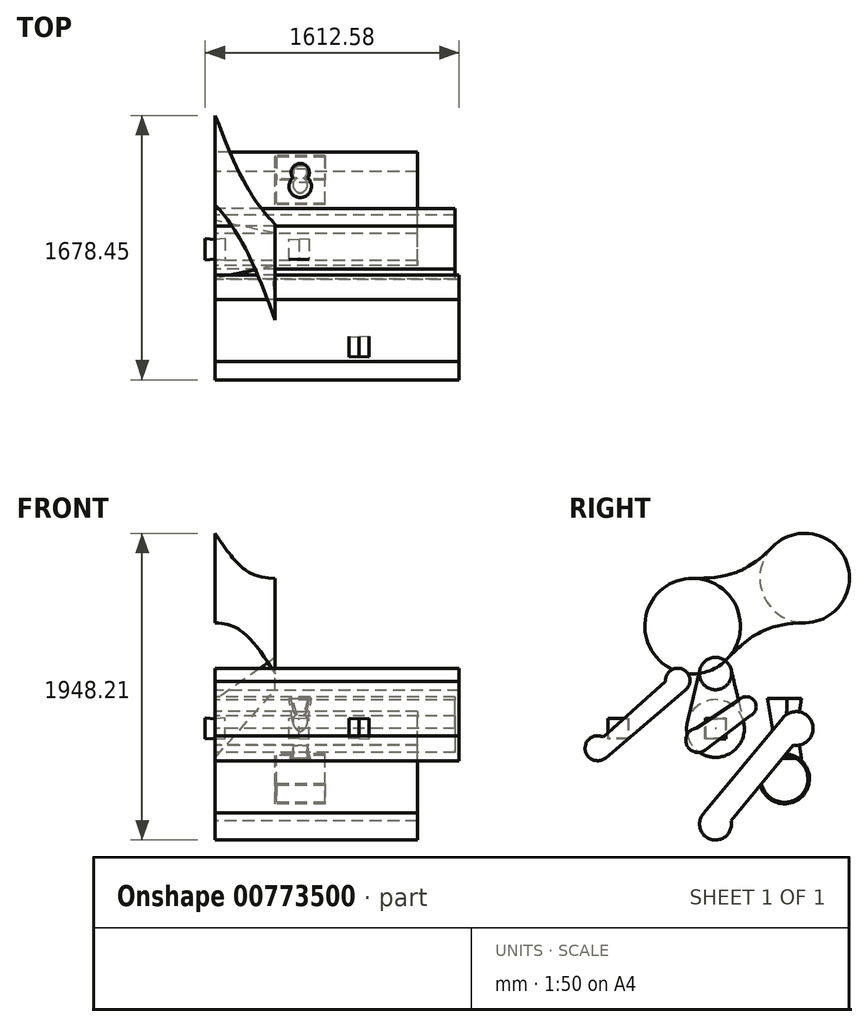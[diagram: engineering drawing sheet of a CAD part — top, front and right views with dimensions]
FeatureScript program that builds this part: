
annotation { "Feature Type Name" : "Feature", "Feature Type Description" : "" }
export const myFeature = defineFeature(function(context is Context, id is Id, definition is map)
    precondition{}
    {
        {
            var Q0;
            Q0=qCreatedBy(makeId("Right.planeOp"),FACE);
            var sketch = newSketch(context, id + "F0", { "sketchPlane" : qUnion([Q0])});
            skArc(sketch, "E0", {"start": v(218.18, 79.74) * mm, "mid": v(247.67, 174.38) * mm, "end": v(148.83, 181.9) * mm});
            skCircle(sketch, "E1", {"center": v(-111.14, -74.72) * mm, "radius": 77.61 * mm});
            skLineSegment(sketch, "E2", {"start": v(218.18, 79.74) * mm, "end": v(-63.95, -136.34) * mm});
            skPoint(sketch, "E3.end.orphan", {"position": v(-138.22, 0) * mm});
            skLineSegment(sketch, "E4", {"start": v(-125.4, 1.57) * mm, "end": v(148.83, 181.9) * mm});
            skSolve(sketch);
        }
        {
            var Q0;
            Q0 = qSketchRegion(id + "F0", true);
            extrude(context, id + "F1", {"entities" : qUnion([Q0]), "depth" : 1524 * mm, "offsetDistance" : 25.4 * mm});
        }
        {
            var Q0;
            Q0=qCreatedBy(makeId("Right.planeOp"),FACE);
            var sketch = newSketch(context, id + "F2", { "sketchPlane" : qUnion([Q0])});
            skCircle(sketch, "E5", {"center": v(-748.62, -125.15) * mm, "radius": 79.46 * mm});
            skCircle(sketch, "E6", {"center": v(-240.04, 305.06) * mm, "radius": 77.83 * mm});
            skLineSegment(sketch, "E7", {"start": v(-192.7, 243.28) * mm, "end": v(-697.14, -185.68) * mm});
            skLineSegment(sketch, "E8", {"start": v(-317.74, 300.55) * mm, "end": v(-712.8, -54.22) * mm});
            skSolve(sketch);
        }
        {
            var Q0;
            Q0 = qSketchRegion(id + "F2", true);
            extrude(context, id + "F3", {"entities" : qUnion([Q0]), "depth" : 1549.08 * mm, "offsetDistance" : 25.4 * mm});
        }
        {
            var Q0;
            Q0=qCreatedBy(makeId("Right.planeOp"),FACE);
            var sketch = newSketch(context, id + "F4", { "sketchPlane" : qUnion([Q0])});
            skCircle(sketch, "E9", {"center": v(511.78, 0) * mm, "radius": 107.3 * mm});
            skCircle(sketch, "E10", {"center": v(0, -606.9) * mm, "radius": 101.16 * mm});
            skLineSegment(sketch, "E11", {"start": v(-72.14, -535.98) * mm, "end": v(429.2, 68.5) * mm});
            skLineSegment(sketch, "E12", {"start": v(99.25, -587.3) * mm, "end": v(493.66, -105.75) * mm});
            skSolve(sketch);
        }
        {
            var Q0;
            Q0 = qSketchRegion(id + "F4", true);
            extrude(context, id + "F5", {"entities" : qUnion([Q0]), "depth" : 1284.3 * mm, "offsetDistance" : 25.4 * mm});
        }
        {
            var Q0;
            Q0=qCreatedBy(makeId("Right.planeOp"),FACE);
            cPlane(context, id + "F6", {"entities" : qUnion([Q0]), "cplaneType" : CPlaneType.OFFSET, "offset" : 381 * mm, "width" : 152.4 * mm, "height" : 152.4 * mm});
        }
        {
            var Q0;
            Q0=qCreatedBy(makeId("Right.planeOp"),FACE);
            var sketch = newSketch(context, id + "F7", { "sketchPlane" : qUnion([Q0])});
            skCircle(sketch, "E13", {"center": v(566.14, 955.92) * mm, "radius": 284.23 * mm});
            skSolve(sketch);
        }
        {
            var Q0;
            Q0=qCreatedBy(id+"F6.planeOp",FACE);
            var sketch = newSketch(context, id + "F8", { "sketchPlane" : qUnion([Q0])});
            skCircle(sketch, "E14", {"center": v(-145.34, 650.7) * mm, "radius": 303.5 * mm});
            skSolve(sketch);
        }
        {
            var Q1;
            Q1=makeQuery(id+"F7.imprint","IMPRINT",FACE,{"disambiguationData":[TD([[makeQuery(id+"F7.imprint","IMPRINT",EDGE,{"derivedFrom":sQuery(id+"F7.wireOp",EDGE,"E13")}),1.0]])]});
            var Q2;
            Q2=makeQuery(id+"F8.imprint","IMPRINT",FACE,{"disambiguationData":[TD([[makeQuery(id+"F8.imprint","IMPRINT",EDGE,{"derivedFrom":sQuery(id+"F8.wireOp",EDGE,"E14")}),1.0]])]});
            loft(context, id + "F9", {"operationType" : NewBodyOperationType.ADD, "sheetProfilesArray" : [{ "sheetProfileEntities" : qUnion([Q1]) }, { "sheetProfileEntities" : qUnion([Q2]) }]});
        }
        {
            var Q0;
            Q0=qCreatedBy(id+"F6.planeOp",FACE);
            var sketch = newSketch(context, id + "F10", { "sketchPlane" : qUnion([Q0])});
            skCircle(sketch, "E15", {"center": v(0, 348.94) * mm, "radius": 102.64 * mm});
            skLineSegment(sketch, "E16", {"start": v(0, 348.94) * mm, "end": v(0, 0) * mm, "construction": true});
            skCircle(sketch, "E17", {"center": v(0, 0) * mm, "radius": 183.3 * mm});
            skSolve(sketch);
        }
        {
            var Q0;
            Q0=qCreatedBy(makeId("Right.planeOp"),FACE);
            var sketch = newSketch(context, id + "F11", { "sketchPlane" : qUnion([Q0])});
            skCircle(sketch, "E18.0", {"center": v(0, 0) * mm, "radius": 183.3 * mm});
            skSolve(sketch);
        }
        {
            var Q0;
            Q0=makeQuery(id+"F11.imprint","IMPRINT",FACE,{"disambiguationData":[TD([[makeQuery(id+"F11.imprint","IMPRINT",EDGE,{"derivedFrom":sQuery(id+"F11.wireOp",EDGE,"E18.0")}),1.0]])]});
            var Q1;
            Q1=makeQuery(id+"F10.imprint","IMPRINT",FACE,{"disambiguationData":[TD([[makeQuery(id+"F10.imprint","IMPRINT",EDGE,{"derivedFrom":sQuery(id+"F10.wireOp",EDGE,"E15")}),1.0]])]});
            loft(context, id + "F12", {"sheetProfilesArray" : [{ "sheetProfileEntities" : qUnion([Q0]) }, { "sheetProfileEntities" : qUnion([Q1]) }]});
        }
        {
            var Q0;
            Q0=qCreatedBy(id+"F6.planeOp",FACE);
            var sketch = newSketch(context, id + "F13", { "sketchPlane" : qUnion([Q0])});
            skLineSegment(sketch, "E19", {"start": v(0, 0) * mm, "end": v(438.16, -319.98) * mm, "construction": true});
            skCircle(sketch, "E20", {"center": v(438.16, -319.98) * mm, "radius": 158.42 * mm});
            skSolve(sketch);
        }
        {
            var Q0;
            Q0 = qSketchRegion(id + "F13", true);
            extrude(context, id + "F14", {"entities" : qUnion([Q0]), "depth" : 316.85 * mm, "offsetDistance" : 25.4 * mm});
        }
        {
            var Q0;
            Q0=makeQuery(id+"F14.opExtrude","CAP_FACE",FACE,{"disambiguationData":[OSD([sQuery(id+"F13.wireOp",EDGE,"E20")])],"isStart":false});
            shell(context, id + "F15", {"entities" : qUnion([Q0]), "thickness" : 9.52 * mm});
        }
        {
            var Q0;
            Q0=qCreatedBy(makeId("Top.planeOp"),FACE);
            var sketch = newSketch(context, id + "F16", { "sketchPlane" : qUnion([Q0])});
            skLineSegment(sketch, "E21", {"start": v(381, 596.58) * mm, "end": v(697.85, 596.58) * mm});
            skLineSegment(sketch, "E22", {"start": v(697.85, 279.74) * mm, "end": v(381, 279.74) * mm});
            skCircle(sketch, "E23", {"center": v(539.42, 400.75) * mm, "radius": 39.96 * mm});
            skPoint(sketch, "E23.centerSnap0", {"position": v(539.42, 596.58) * mm});
            skCircle(sketch, "E24", {"center": v(539.42, 487.87) * mm, "radius": 26.5 * mm});
            skSolve(sketch);
        }
        {
            var Q0;
            Q0 = qSketchRegion(id + "F16", true);
            extrude(context, id + "F17", {"entities" : qUnion([Q0]), "operationType" : NewBodyOperationType.ADD, "endBound" : BoundingType.SYMMETRIC, "depth" : 381 * mm, "offsetDistance" : 25.4 * mm, "hasDraft" : true, "draftAngle" : 9.38 * degree});
        }
        {
            var Q0;
            Q0=qCreatedBy(makeId("Top.planeOp"),FACE);
            var sketch = newSketch(context, id + "F18", { "sketchPlane" : qUnion([Q0])});
            skLineSegment(sketch, "E25", {"start": v(0, 0) * mm, "end": v(0, -609.6) * mm, "construction": true});
            skLineSegment(sketch, "E26", {"start": v(0, -609.6) * mm, "end": v(914.4, -609.6) * mm, "construction": true});
            skSolve(sketch);
        }
        {
            var Q0;
            Q0=qCreatedBy(makeId("Right.planeOp"),FACE);
            var Q1;
            Q1=sQuery(id+"F18.wireOp",VERTEX,"E26.end");
            cPlane(context, id + "F19", {"entities" : qUnion([Q0, Q1]), "cplaneType" : CPlaneType.PLANE_POINT, "offset" : 25.4 * mm, "width" : 152.4 * mm, "height" : 152.4 * mm});
        }
        {
            var Q0;
            Q0=qCreatedBy(id+"F19.planeOp",FACE);
            var sketch = newSketch(context, id + "F20", { "sketchPlane" : qUnion([Q0])});
            skLineSegment(sketch, "E27.bottom", {"start": v(-679.03, -61.91) * mm, "end": v(-555.2, -61.91) * mm});
            skLineSegment(sketch, "E27.top", {"start": v(-679.03, 61.91) * mm, "end": v(-555.2, 61.91) * mm});
            skLineSegment(sketch, "E27.left", {"start": v(-679.03, -61.91) * mm, "end": v(-679.03, 61.91) * mm});
            skLineSegment(sketch, "E27.right", {"start": v(-555.2, -61.91) * mm, "end": v(-555.2, 61.91) * mm});
            skPoint(sketch, "E27.middle", {"position": v(-617.11, 0) * mm});
            skLineSegment(sketch, "E28.bottom", {"start": v(-61.91, -61.91) * mm, "end": v(61.91, -61.91) * mm});
            skLineSegment(sketch, "E28.top", {"start": v(-61.91, 61.91) * mm, "end": v(61.91, 61.91) * mm});
            skLineSegment(sketch, "E28.left", {"start": v(-61.91, -61.91) * mm, "end": v(-61.91, 61.91) * mm});
            skLineSegment(sketch, "E28.right", {"start": v(61.91, -61.91) * mm, "end": v(61.91, 61.91) * mm});
            skPoint(sketch, "E28.middle", {"position": v(0, 0) * mm});
            skSolve(sketch);
        }
        {
            var Q0;
            Q0 = qSketchRegion(id + "F20", true);
            extrude(context, id + "F21", {"entities" : qUnion([Q0]), "endBound" : BoundingType.SYMMETRIC, "depth" : 127 * mm, "offsetDistance" : 25.4 * mm, "hasDraft" : true, "draftAngle" : 3 * degree});
        }
        {
            var Q0;
            Q0=makeQuery(id+"F21.*.split.splitOp","SPLIT",BODY,{"derivedFrom":makeQuery(id+"F21.opExtrude","SWEPT_BODY",BODY,{"disambiguationData":[OSD([sQuery(id+"F20.wireOp",EDGE,"E28.bottom"),sQuery(id+"F20.wireOp",EDGE,"E28.top"),sQuery(id+"F20.wireOp",EDGE,"E28.left"),sQuery(id+"F20.wireOp",EDGE,"E28.right")])]})});
            transform(context, id + "F22", {"entities" : qUnion([Q0]), "transformType" : TransformType.TRANSLATION_3D, "dx" : -381 * mm, "dy" : 0 * mm, "dz" : 0 * mm, "makeCopy" : false});
        }
        {
            var Q0;
            Q0=qCreatedBy(makeId("Right.planeOp"),FACE);
            var sketch = newSketch(context, id + "F23", { "sketchPlane" : qUnion([Q0])});
            skLineSegment(sketch, "E29.bottom", {"start": v(-61.91, -61.91) * mm, "end": v(61.91, -61.91) * mm});
            skLineSegment(sketch, "E29.top", {"start": v(-61.91, 61.91) * mm, "end": v(61.91, 61.91) * mm});
            skLineSegment(sketch, "E29.left", {"start": v(-61.91, -61.91) * mm, "end": v(-61.91, 61.91) * mm});
            skLineSegment(sketch, "E29.right", {"start": v(61.91, -61.91) * mm, "end": v(61.91, 61.91) * mm});
            skPoint(sketch, "E29.middle", {"position": v(0, 0) * mm});
            skSolve(sketch);
        }
        {
            var Q0;
            Q0=makeQuery(id+"F23.imprint","IMPRINT",FACE,{"disambiguationData":[TD([[makeQuery(id+"F23.imprint","IMPRINT",EDGE,{"derivedFrom":sQuery(id+"F23.wireOp",EDGE,"E29.bottom")}),1.0]])]});
            var Q1;
            Q1=sQuery(id+"F23.wireOp",EDGE,"E29.top");
            var Q2;
            Q2=sQuery(id+"F23.wireOp",EDGE,"E29.left");
            var Q3;
            Q3=sQuery(id+"F23.wireOp",EDGE,"E29.right");
            extrude(context, id + "F24", {"entities" : qUnion([Q0]), "surfaceEntities" : qUnion([Q1, Q2, Q3]), "endBound" : BoundingType.SYMMETRIC, "depth" : 127 * mm, "offsetDistance" : 25.4 * mm, "hasDraft" : true, "draftAngle" : 5 * degree});
        }
        {
            var Q0;
            Q0=qCreatedBy(makeId("Top.planeOp"),FACE);
            var sketch = newSketch(context, id + "F25", { "sketchPlane" : qUnion([Q0])});
            skLineSegment(sketch, "E30.bottom", {"start": v(1.27, -1.27) * mm, "end": v(-1.27, -1.27) * mm});
            skLineSegment(sketch, "E30.top", {"start": v(1.27, 1.27) * mm, "end": v(-1.27, 1.27) * mm});
            skLineSegment(sketch, "E30.left", {"start": v(1.27, -1.27) * mm, "end": v(1.27, 1.27) * mm});
            skLineSegment(sketch, "E30.right", {"start": v(-1.27, -1.27) * mm, "end": v(-1.27, 1.27) * mm});
            skPoint(sketch, "E30.middle", {"position": v(0, 0) * mm});
            skSolve(sketch);
        }
        {
            var Q0;
            Q0 = qSketchRegion(id + "F25", true);
            extrude(context, id + "F26", {"entities" : qUnion([Q0]), "depth" : 2.54 * mm, "offsetDistance" : 25.4 * mm});
        }
    });
